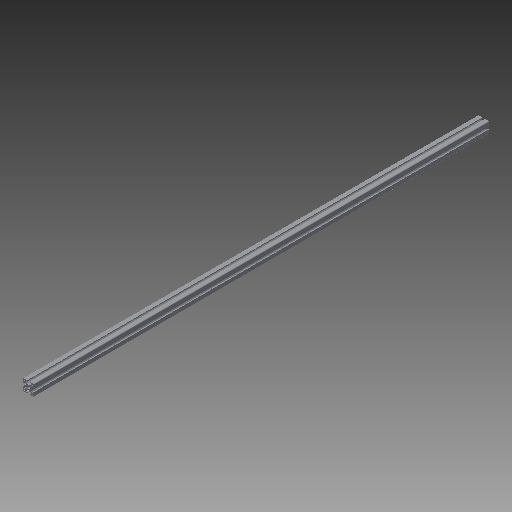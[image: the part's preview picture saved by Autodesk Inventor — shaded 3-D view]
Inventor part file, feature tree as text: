
AUTODESK INVENTOR PART (.ipt)
format: ipt  version: 2018 (Build 220112000, 112)  size: 220,672 bytes
history: native  units: mm
features: other x42, sketch x5, hole x4, extrude x1
ambient origin geometry x8: Origin, YZ Plane, XZ Plane, XY Plane, X Axis, Y Axis, Z Axis, Center Point
bodies: Solid1 (feature_tree)
feature tree (52):
  extrude  "Extrusion1"  [1 undecoded]
  hole  "Drilling 1"  [1 undecoded]
  hole  "Drilling 2"  [1 undecoded]
  hole  "Drilling 3"  [1 undecoded]
  hole  "Drilling 4"  [1 undecoded]
  other  "side_4d_XY"
  other  "side_4d_YZ"
  other  "side_4d_ZX"
  other  "side_4d_X"
  other  "side_4d_Y"
  other  "side_4d_Z"
  other  "side_4d_Center"
  other  "side_1a_XY"
  other  "side_1a_YZ"
  other  "side_1a_ZX"
  other  "side_1a_X"
  other  "side_1a_Y"
  other  "side_1a_Z"
  other  "side_1a_Center"
  other  "side_2b_XY"
  other  "side_2b_YZ"
  other  "side_2b_ZX"
  other  "side_2b_X"
  other  "side_2b_Y"
  other  "side_2b_Z"
  other  "side_2b_Center"
  other  "side_3c_XY"
  other  "side_3c_YZ"
  other  "side_3c_ZX"
  other  "side_3c_X"
  other  "side_3c_Y"
  other  "side_3c_Z"
  other  "side_3c_Center"
  other  "end_XY"
  other  "end_YZ"
  other  "end_ZX"
  other  "end_X"
  other  "end_Y"
  other  "end_Z"
  other  "end_Center"
  other  "start_XY"
  other  "start_YZ"
  other  "start_ZX"
  other  "start_X"
  other  "start_Y"
  other  "start_Z"
  other  "start_Center"
  sketch  "Skizze_1"  dims[d0=1627.0mm d1=0.0mm]
  sketch  "Sketch2"  dims[d2=5.0mm d3=6.0mm d4=4.0mm d5=2.0mm d6=90.0deg d7=6000.0mm d8=0.0mm]
  sketch  "Sketch3"  dims[d9=5.0mm d10=6.0mm d11=4.0mm d12=2.0mm d13=90.0deg d14=6000.0mm d15=0.0mm]
  sketch  "Sketch4"  dims[d16=5.0mm d17=6.0mm d18=4.0mm d19=2.0mm d20=90.0deg d21=6000.0mm d22=0.0mm]
  sketch  "Sketch5"  dims[d23=5.0mm d24=6.0mm d25=4.0mm d26=2.0mm d27=90.0deg d28=6000.0mm d29=0.0mm]
note: 5 required parameter values undecoded (feature->parameter linkage not recoverable at this tier; creation-order binding heuristic only, values carry confidence <= 0.55)
